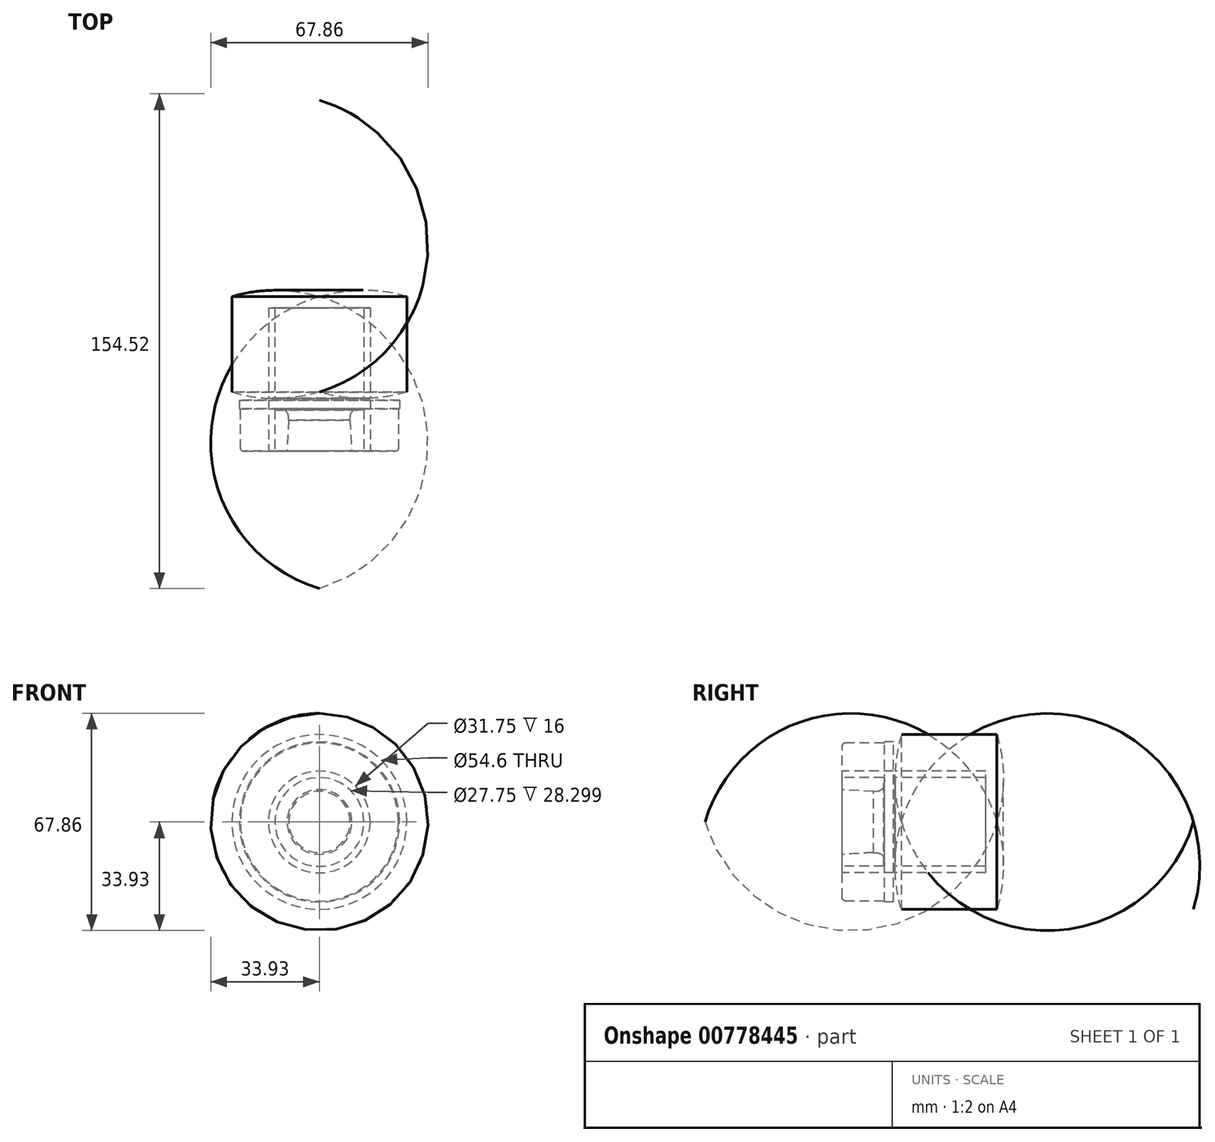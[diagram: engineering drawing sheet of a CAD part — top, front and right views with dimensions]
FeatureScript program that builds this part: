
annotation { "Feature Type Name" : "Feature", "Feature Type Description" : "" }
export const myFeature = defineFeature(function(context is Context, id is Id, definition is map)
    precondition{}
    {
        {
            var Q0;
            Q0=qCreatedBy(makeId("Right.planeOp"),FACE);
            var sketch = newSketch(context, id + "F0", { "sketchPlane" : qUnion([Q0])});
            skLineSegment(sketch, "E0", {"start": v(-17.8, 0) * mm, "end": v(382.15, 0) * mm, "construction": true});
            skLineSegment(sketch, "E1", {"start": v(0, 23.68) * mm, "end": v(0, 10.1) * mm});
            skLineSegment(sketch, "E2", {"start": v(50.3, 27.3) * mm, "end": v(16.5, 27.3) * mm});
            skLineSegment(sketch, "E3", {"start": v(44.8, 15.88) * mm, "end": v(0, 15.88) * mm});
            skLineSegment(sketch, "E4", {"start": v(44.8, 13.88) * mm, "end": v(0, 13.88) * mm});
            skLineSegment(sketch, "E5", {"start": v(50.8, 26.8) * mm, "end": v(50.8, -26.8) * mm});
            skLineSegment(sketch, "E6", {"start": v(16, 26.8) * mm, "end": v(16, -26.8) * mm});
            skLineSegment(sketch, "E7", {"start": v(16, 25) * mm, "end": v(13.25, 25) * mm});
            skLineSegment(sketch, "E8", {"start": v(44.8, 16) * mm, "end": v(44.8, -16) * mm});
            skLineSegment(sketch, "E9", {"start": v(50.8, 16) * mm, "end": v(44.8, 16) * mm});
            skLineSegment(sketch, "E10", {"start": v(50.3, -27.3) * mm, "end": v(16.5, -27.3) * mm});
            skLineSegment(sketch, "E11", {"start": v(16, -25) * mm, "end": v(13.25, -25) * mm});
            skLineSegment(sketch, "E12", {"start": v(44.8, -15.88) * mm, "end": v(0, -15.88) * mm});
            skLineSegment(sketch, "E13", {"start": v(44.8, -13.88) * mm, "end": v(0, -13.88) * mm});
            skLineSegment(sketch, "E14", {"start": v(50.8, -16) * mm, "end": v(44.8, -16) * mm});
            skLineSegment(sketch, "E15", {"start": v(18.5, 0) * mm, "end": v(48.3, 0) * mm});
            skArc(sketch, "E16", {"start": v(48.3, 0) * mm, "mid": v(50.3, 13.65) * mm, "end": v(48.3, 27.3) * mm});
            skLineSegment(sketch, "E17", {"start": v(50.3, 27.3) * mm, "end": v(50.8, 26.8) * mm});
            skLineSegment(sketch, "E18", {"start": v(50.8, -26.8) * mm, "end": v(50.3, -27.3) * mm});
            skArc(sketch, "E19", {"start": v(48.3, -27.3) * mm, "mid": v(50.3, -13.65) * mm, "end": v(48.3, 0) * mm});
            skArc(sketch, "E20", {"start": v(18.5, 27.3) * mm, "mid": v(16.5, 13.65) * mm, "end": v(18.5, 0) * mm});
            skArc(sketch, "E21", {"start": v(18.5, 0) * mm, "mid": v(16.5, -13.65) * mm, "end": v(18.5, -27.3) * mm});
            skLineSegment(sketch, "E22", {"start": v(16.5, 27.3) * mm, "end": v(16, 26.8) * mm});
            skLineSegment(sketch, "E23", {"start": v(16.5, -27.3) * mm, "end": v(16, -26.8) * mm});
            skLineSegment(sketch, "E24", {"start": v(13, 24.68) * mm, "end": v(1, 24.68) * mm});
            skLineSegment(sketch, "E25", {"start": v(13.25, 12.14) * mm, "end": v(13.25, 12.65) * mm});
            skLineSegment(sketch, "E26", {"start": v(0, 15.8) * mm, "end": v(10.9, 15.15) * mm});
            skLineSegment(sketch, "E27", {"start": v(10.93, 9.65) * mm, "end": v(0, 8.87) * mm});
            skArc(sketch, "E28", {"start": v(13.25, 12.65) * mm, "mid": v(12.57, 14.37) * mm, "end": v(10.9, 15.15) * mm});
            skArc(sketch, "E29", {"start": v(10.93, 9.65) * mm, "mid": v(12.58, 10.44) * mm, "end": v(13.25, 12.14) * mm});
            skLineSegment(sketch, "E30", {"start": v(13.25, 6.5) * mm, "end": v(13.25, 7) * mm});
            skLineSegment(sketch, "E31", {"start": v(0, 10.1) * mm, "end": v(9.76, 9.57) * mm});
            skLineSegment(sketch, "E32", {"start": v(0, 3.18) * mm, "end": v(10.94, 4) * mm});
            skArc(sketch, "E33", {"start": v(13.25, 7) * mm, "mid": v(12.57, 8.72) * mm, "end": v(10.89, 9.5) * mm});
            skArc(sketch, "E34", {"start": v(10.94, 4) * mm, "mid": v(12.58, 4.8) * mm, "end": v(13.25, 6.5) * mm});
            skLineSegment(sketch, "E35", {"start": v(9.76, 9.57) * mm, "end": v(10.89, 9.5) * mm});
            skLineSegment(sketch, "E36", {"start": v(13.25, 25) * mm, "end": v(13.25, 24.93) * mm});
            skArc(sketch, "E37", {"start": v(1, 24.68) * mm, "mid": v(0.3, 24.39) * mm, "end": v(0, 23.68) * mm});
            skArc(sketch, "E38", {"start": v(13, 24.68) * mm, "mid": v(13.18, 24.75) * mm, "end": v(13.25, 24.93) * mm});
            skArc(sketch, "E39", {"start": v(0, -23.68) * mm, "mid": v(0.3, -24.39) * mm, "end": v(1, -24.68) * mm});
            skLineSegment(sketch, "E40", {"start": v(13, -24.68) * mm, "end": v(1, -24.68) * mm});
            skLineSegment(sketch, "E41", {"start": v(13.25, -12.14) * mm, "end": v(13.25, -12.65) * mm});
            skArc(sketch, "E42", {"start": v(13.25, -12.14) * mm, "mid": v(12.58, -10.44) * mm, "end": v(10.93, -9.65) * mm});
            skArc(sketch, "E43", {"start": v(10.9, -15.15) * mm, "mid": v(12.57, -14.37) * mm, "end": v(13.25, -12.65) * mm});
            skLineSegment(sketch, "E44", {"start": v(0, -15.8) * mm, "end": v(10.9, -15.15) * mm});
            skLineSegment(sketch, "E45", {"start": v(10.93, -9.65) * mm, "end": v(0, -8.87) * mm});
            skLineSegment(sketch, "E46", {"start": v(13.25, -6.5) * mm, "end": v(13.25, -7) * mm});
            skArc(sketch, "E47", {"start": v(13.25, -6.5) * mm, "mid": v(12.58, -4.8) * mm, "end": v(10.94, -4) * mm});
            skArc(sketch, "E48", {"start": v(10.89, -9.5) * mm, "mid": v(12.57, -8.72) * mm, "end": v(13.25, -7) * mm});
            skLineSegment(sketch, "E49", {"start": v(0, -10.1) * mm, "end": v(9.76, -9.57) * mm});
            skLineSegment(sketch, "E50", {"start": v(9.76, -9.57) * mm, "end": v(10.89, -9.5) * mm});
            skLineSegment(sketch, "E51", {"start": v(0, -3.18) * mm, "end": v(10.94, -4) * mm});
            skLineSegment(sketch, "E52", {"start": v(13.25, -25) * mm, "end": v(13.25, -24.93) * mm});
            skArc(sketch, "E53", {"start": v(13.25, -24.93) * mm, "mid": v(13.18, -24.75) * mm, "end": v(13, -24.68) * mm});
            skLineSegment(sketch, "E54", {"start": v(0, 8.87) * mm, "end": v(0, -8.87) * mm});
            skLineSegment(sketch, "E55", {"start": v(0, -10.1) * mm, "end": v(0, -23.68) * mm});
            skSolve(sketch);
        }
        {
            var Q0;
            {var subQ1=sQuery(id+"F0.wireOp",EDGE,"E8");var subQ6=makeQuery(id+"F0.imprint","INTERSECT",VERTEX,{"derivedFrom":[subQ1,sQuery(id+"F0.wireOp",EDGE,"E13")]});Q0=makeQuery(id+"F0.imprint","IMPRINT",FACE,{"disambiguationData":[TD([[makeQuery(id+"F0.imprint","IMPRINT",EDGE,{"disambiguationData":[TD([[subQ6,1.0]])],"derivedFrom":subQ1}),1.0]])]});}
            var Q1;
            {var subQ1=sQuery(id+"F0.wireOp",EDGE,"E8");var subQ9=sQuery(id+"F0.wireOp",EDGE,"E14");var subQ10=makeQuery(id+"F0.imprint","INTERSECT",VERTEX,{"derivedFrom":[subQ1,subQ9]});Q1=makeQuery(id+"F0.imprint","IMPRINT",FACE,{"disambiguationData":[TD([[makeQuery(id+"F0.imprint","IMPRINT",EDGE,{"disambiguationData":[TD([[subQ10,1.0]])],"derivedFrom":subQ1}),-1.0]])]});}
            var Q2;
            {var subQ1=sQuery(id+"F0.wireOp",EDGE,"E41");Q2=makeQuery(id+"F0.imprint","IMPRINT",FACE,{"disambiguationData":[TD([[makeQuery(id+"F0.imprint","IMPRINT",EDGE,{"derivedFrom":subQ1}),-1.0]])]});}
            var Q3;
            {var subQ0=sQuery(id+"F0.wireOp",EDGE,"E13");var subQ1=sQuery(id+"F0.wireOp",EDGE,"E8");var subQ2=makeQuery(id+"F0.imprint","INTERSECT",VERTEX,{"derivedFrom":[subQ1,subQ0]});Q3=makeQuery(id+"F0.imprint","IMPRINT",FACE,{"disambiguationData":[TD([[makeQuery(id+"F0.imprint","IMPRINT",EDGE,{"disambiguationData":[TD([[subQ2,1.0]])],"derivedFrom":subQ1}),-1.0]])]});}
            var Q4;
            {var subQ6=sQuery(id+"F0.wireOp",EDGE,"E11");Q4=makeQuery(id+"F0.imprint","IMPRINT",FACE,{"disambiguationData":[TD([[makeQuery(id+"F0.imprint","IMPRINT",EDGE,{"derivedFrom":subQ6}),-1.0]])]});}
            var Q5;
            Q5=sQuery(id+"F0.wireOp",EDGE,"E0");
            revolve(context, id + "F1", {"surfaceOperationType" : NewSurfaceOperationType.NEW, "entities" : qUnion([Q0, Q1, Q2, Q3, Q4]), "axis" : qUnion([Q5]), "revolveType" : RevolveType.FULL});
        }
    });
